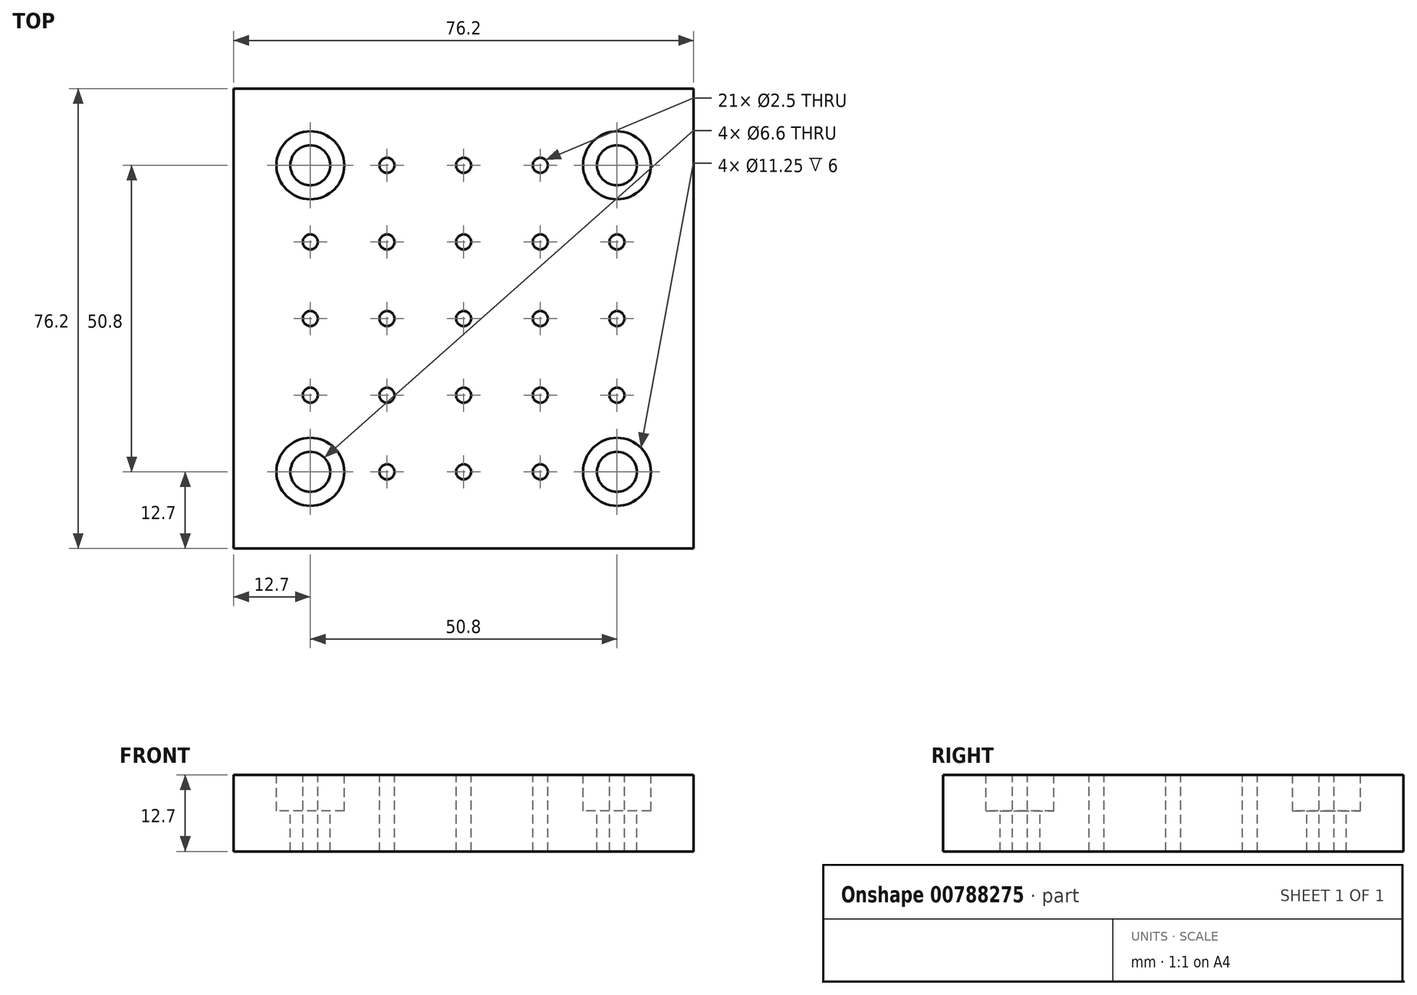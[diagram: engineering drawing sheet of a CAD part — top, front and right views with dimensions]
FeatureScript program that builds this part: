
annotation { "Feature Type Name" : "Feature", "Feature Type Description" : "" }
export const myFeature = defineFeature(function(context is Context, id is Id, definition is map)
    precondition{}
    {
        {
            var Q0;
            Q0=qCreatedBy(makeId("Top.planeOp"),FACE);
            var sketch = newSketch(context, id + "F0", { "sketchPlane" : qUnion([Q0])});
            skLineSegment(sketch, "E0.bottom", {"start": v(-38.1, 38.1) * mm, "end": v(38.1, 38.1) * mm});
            skLineSegment(sketch, "E0.top", {"start": v(-38.1, -38.1) * mm, "end": v(38.1, -38.1) * mm});
            skLineSegment(sketch, "E0.left", {"start": v(-38.1, 38.1) * mm, "end": v(-38.1, -38.1) * mm});
            skLineSegment(sketch, "E0.right", {"start": v(38.1, 38.1) * mm, "end": v(38.1, -38.1) * mm});
            skPoint(sketch, "E0.middle", {"position": v(0, 0) * mm});
            skLineSegment(sketch, "E1", {"start": v(-25.4, 38.1) * mm, "end": v(-25.4, 25.4) * mm, "construction": true});
            skLineSegment(sketch, "E2", {"start": v(-25.4, 25.4) * mm, "end": v(-38.1, 25.4) * mm, "construction": true});
            skPoint(sketch, "E3", {"position": v(-25.4, 25.4) * mm});
            skPoint(sketch, "E4.0.1.0", {"position": v(-25.4, 12.7) * mm});
            skPoint(sketch, "E4.0.2.0", {"position": v(-25.4, 0) * mm});
            skPoint(sketch, "E4.0.3.0", {"position": v(-25.4, -12.7) * mm});
            skPoint(sketch, "E4.0.4.0", {"position": v(-25.4, -25.4) * mm});
            skPoint(sketch, "E4.1.0.0", {"position": v(-12.7, 25.4) * mm});
            skPoint(sketch, "E4.1.1.0", {"position": v(-12.7, 12.7) * mm});
            skPoint(sketch, "E4.1.2.0", {"position": v(-12.7, 0) * mm});
            skPoint(sketch, "E4.1.3.0", {"position": v(-12.7, -12.7) * mm});
            skPoint(sketch, "E4.1.4.0", {"position": v(-12.7, -25.4) * mm});
            skPoint(sketch, "E4.2.0.0", {"position": v(0, 25.4) * mm});
            skPoint(sketch, "E4.2.1.0", {"position": v(0, 12.7) * mm});
            skPoint(sketch, "E4.2.3.0", {"position": v(0, -12.7) * mm});
            skPoint(sketch, "E4.2.4.0", {"position": v(0, -25.4) * mm});
            skPoint(sketch, "E4.3.0.0", {"position": v(12.7, 25.4) * mm});
            skPoint(sketch, "E4.3.1.0", {"position": v(12.7, 12.7) * mm});
            skPoint(sketch, "E4.3.2.0", {"position": v(12.7, 0) * mm});
            skPoint(sketch, "E4.3.3.0", {"position": v(12.7, -12.7) * mm});
            skPoint(sketch, "E4.3.4.0", {"position": v(12.7, -25.4) * mm});
            skPoint(sketch, "E4.4.0.0", {"position": v(25.4, 25.4) * mm});
            skPoint(sketch, "E4.4.1.0", {"position": v(25.4, 12.7) * mm});
            skPoint(sketch, "E4.4.2.0", {"position": v(25.4, 0) * mm});
            skPoint(sketch, "E4.4.3.0", {"position": v(25.4, -12.7) * mm});
            skPoint(sketch, "E4.4.4.0", {"position": v(25.4, -25.4) * mm});
            skLineSegment(sketch, "E4.direction1", {"start": v(-25.4, 25.4) * mm, "end": v(-12.7, 25.4) * mm, "construction": true});
            skLineSegment(sketch, "E4.direction2", {"start": v(-25.4, 25.4) * mm, "end": v(-25.4, 12.7) * mm, "construction": true});
            skSolve(sketch);
        }
        {
            var Q0;
            Q0=makeQuery(id+"F0.imprint","IMPRINT",FACE,{"disambiguationData":[TD([[makeQuery(id+"F0.imprint","IMPRINT",EDGE,{"derivedFrom":sQuery(id+"F0.wireOp",EDGE,"E0.bottom")}),-1.0]])]});
            extrude(context, id + "F1", {"entities" : qUnion([Q0]), "oppositeDirection" : true, "depth" : 12.7 * mm, "offsetDistance" : 25.4 * mm});
        }
        {
            var Q0;
            Q0=sQuery(id+"F0.wireOp",VERTEX,"E4.0.1.0");
            var Q1;
            Q1=sQuery(id+"F0.wireOp",VERTEX,"E4.1.0.0");
            var Q2;
            Q2=sQuery(id+"F0.wireOp",VERTEX,"E4.1.1.0");
            var Q3;
            Q3=sQuery(id+"F0.wireOp",VERTEX,"E4.2.1.0");
            var Q4;
            Q4=sQuery(id+"F0.wireOp",VERTEX,"E4.3.0.0");
            var Q5;
            Q5=sQuery(id+"F0.wireOp",VERTEX,"E4.2.0.0");
            var Q6;
            Q6=sQuery(id+"F0.wireOp",VERTEX,"E4.3.1.0");
            var Q7;
            Q7=sQuery(id+"F0.wireOp",VERTEX,"E4.4.1.0");
            var Q8;
            Q8=sQuery(id+"F0.wireOp",VERTEX,"E4.4.2.0");
            var Q9;
            Q9=sQuery(id+"F0.wireOp",VERTEX,"E4.3.2.0");
            var Q10;
            Q10=sQuery(id+"F0.wireOp",VERTEX,"E0.middle");
            var Q11;
            Q11=sQuery(id+"F0.wireOp",VERTEX,"E4.1.2.0");
            var Q12;
            Q12=sQuery(id+"F0.wireOp",VERTEX,"E4.0.2.0");
            var Q13;
            Q13=sQuery(id+"F0.wireOp",VERTEX,"E4.0.3.0");
            var Q14;
            Q14=sQuery(id+"F0.wireOp",VERTEX,"E4.1.3.0");
            var Q15;
            Q15=sQuery(id+"F0.wireOp",VERTEX,"E4.2.3.0");
            var Q16;
            Q16=sQuery(id+"F0.wireOp",VERTEX,"E4.3.3.0");
            var Q17;
            Q17=sQuery(id+"F0.wireOp",VERTEX,"E4.4.3.0");
            var Q18;
            Q18=sQuery(id+"F0.wireOp",VERTEX,"E4.3.4.0");
            var Q19;
            Q19=sQuery(id+"F0.wireOp",VERTEX,"E4.2.4.0");
            var Q20;
            Q20=sQuery(id+"F0.wireOp",VERTEX,"E4.1.4.0");
            var Q21;
            Q21=makeQuery(id+"F1.opExtrude","SWEPT_BODY",BODY,{"disambiguationData":[OSD([sQuery(id+"F0.wireOp",EDGE,"E0.bottom"),sQuery(id+"F0.wireOp",EDGE,"E0.top"),sQuery(id+"F0.wireOp",EDGE,"E0.left"),sQuery(id+"F0.wireOp",EDGE,"E0.right")])]});
            hole(context, id + "F2", {"style" : HoleStyle.SIMPLE, "endStyle" : HoleEndStyle.THROUGH, "standardTappedOrClearance" : lookupTablePath({ "standard" : "ISO", "engagement" : "75%", "pitch" : "0.5 mm", "size" : "M3", "type" : "Tapped" }), "standardBlindInLast" : lookupTablePath({ "standard" : "ISO", "engagement" : "75%", "pitch" : "0.5 mm", "size" : "M3", "type" : "Tapped" }), "holeDiameter" : 2.5 * mm, "majorDiameter" : 3 * mm, "showTappedDepth" : true, "isTappedThrough" : true, "tappedDepth" : 12.7 * mm, "tapClearance" : 3, "locations" : qUnion([Q0, Q1, Q2, Q3, Q4, Q5, Q6, Q7, Q8, Q9, Q10, Q11, Q12, Q13, Q14, Q15, Q16, Q17, Q18, Q19, Q20]), "scope" : qUnion([Q21])});
        }
        {
            var Q0;
            Q0=sQuery(id+"F0.wireOp",VERTEX,"E3");
            var Q1;
            Q1=sQuery(id+"F0.wireOp",VERTEX,"E4.4.0.0");
            var Q2;
            Q2=sQuery(id+"F0.wireOp",VERTEX,"E4.4.4.0");
            var Q3;
            Q3=sQuery(id+"F0.wireOp",VERTEX,"E4.0.4.0");
            var Q4;
            Q4=makeQuery(id+"F1.opExtrude","SWEPT_BODY",BODY,{"disambiguationData":[OSD([sQuery(id+"F0.wireOp",EDGE,"E0.bottom"),sQuery(id+"F0.wireOp",EDGE,"E0.top"),sQuery(id+"F0.wireOp",EDGE,"E0.left"),sQuery(id+"F0.wireOp",EDGE,"E0.right")])]});
            hole(context, id + "F3", {"style" : HoleStyle.C_BORE, "endStyle" : HoleEndStyle.THROUGH, "standardTappedOrClearance" : lookupTablePath({ "standard" : "ISO", "fit" : "Normal", "size" : "M6", "type" : "Clearance" }), "standardBlindInLast" : lookupTablePath({ "fit" : "Standard", "standard" : "ISO", "size" : "M6", "type" : "Clearance" }), "holeDiameter" : 6.6 * mm, "cBoreDiameter" : 11.25 * mm, "cBoreDepth" : 6 * mm, "majorDiameter" : 6 * mm, "isTappedThrough" : true, "tappedDepth" : 12.7 * mm, "tapClearance" : 3, "locations" : qUnion([Q0, Q1, Q2, Q3]), "scope" : qUnion([Q4])});
        }
    });
